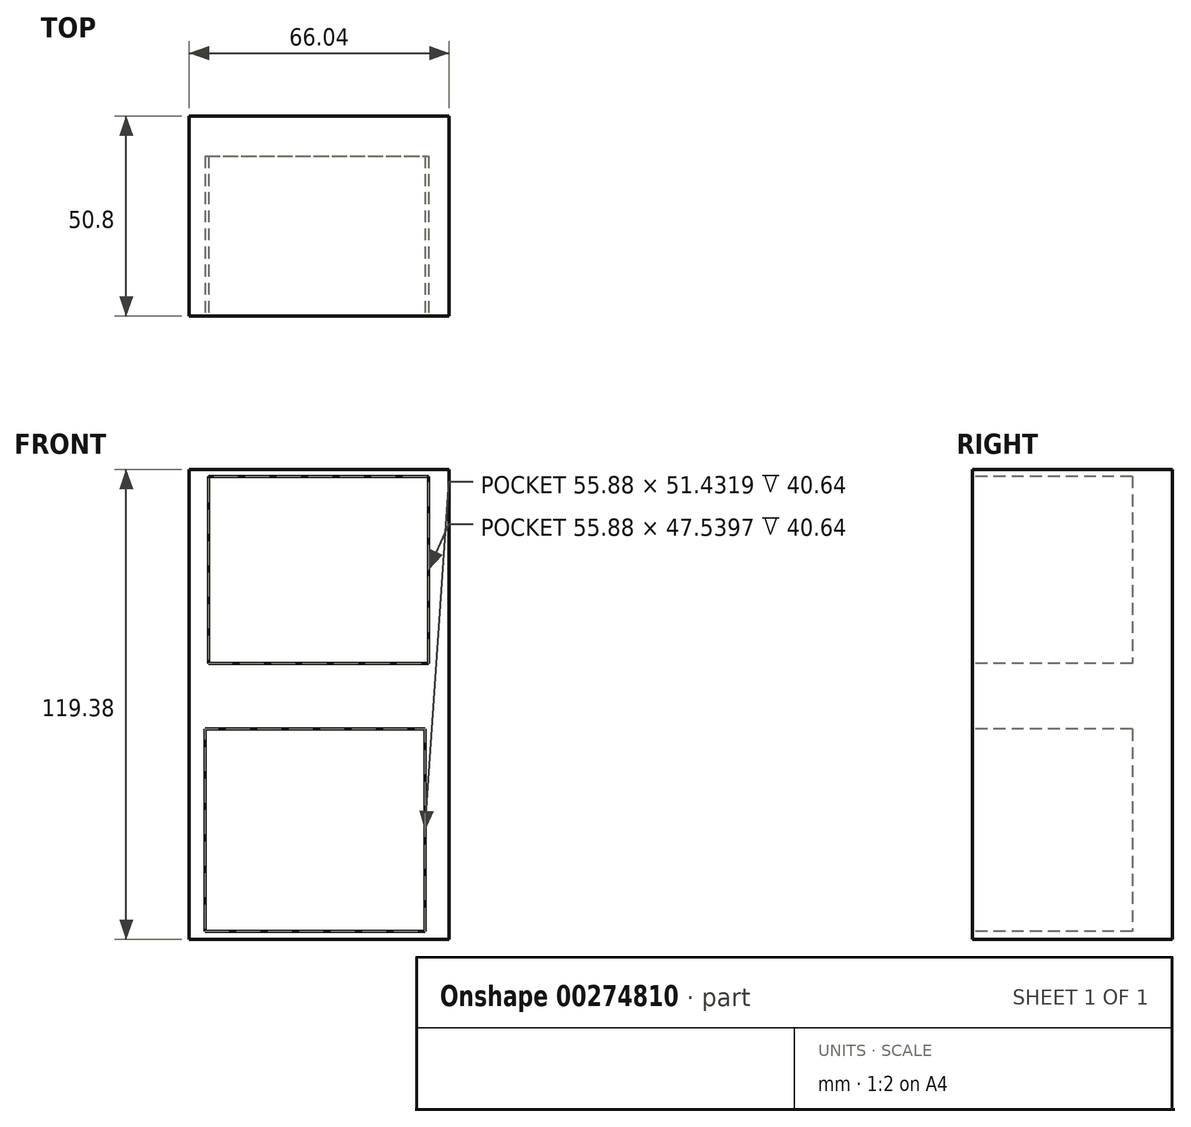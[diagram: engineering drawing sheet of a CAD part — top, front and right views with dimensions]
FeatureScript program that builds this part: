
annotation { "Feature Type Name" : "Feature", "Feature Type Description" : "" }
export const myFeature = defineFeature(function(context is Context, id is Id, definition is map)
    precondition{}
    {
        {
            var Q0;
            Q0=qCreatedBy(makeId("Front.planeOp"),FACE);
            var sketch = newSketch(context, id + "F0", { "sketchPlane" : qUnion([Q0])});
            skLineSegment(sketch, "E0.bottom", {"start": v(33.02, -59.69) * mm, "end": v(-33.02, -59.7) * mm});
            skLineSegment(sketch, "E0.top", {"start": v(33.02, 59.7) * mm, "end": v(-33.02, 59.69) * mm});
            skLineSegment(sketch, "E0.left", {"start": v(33.02, -59.69) * mm, "end": v(33.02, 59.7) * mm});
            skLineSegment(sketch, "E0.right", {"start": v(-33.02, -59.7) * mm, "end": v(-33.02, 59.69) * mm});
            skPoint(sketch, "E0.middle", {"position": v(0, 0) * mm});
            skSolve(sketch);
        }
        {
            var Q0;
            Q0=makeQuery(id+"F0.imprint","IMPRINT",FACE,{"disambiguationData":[TD([[makeQuery(id+"F0.imprint","IMPRINT",EDGE,{"derivedFrom":sQuery(id+"F0.wireOp",EDGE,"E0.bottom")}),-1.0]])]});
            extrude(context, id + "F1", {"entities" : qUnion([Q0]), "depth" : 50.8 * mm});
        }
        {
            var Q0;
            Q0=makeQuery(id+"F1.opExtrude","CAP_FACE",FACE,{"disambiguationData":[OSD([sQuery(id+"F0.wireOp",EDGE,"E0.bottom"),sQuery(id+"F0.wireOp",EDGE,"E0.top"),sQuery(id+"F0.wireOp",EDGE,"E0.left"),sQuery(id+"F0.wireOp",EDGE,"E0.right")])],"isStart":false});
            var sketch = newSketch(context, id + "F2", { "sketchPlane" : qUnion([Q0])});
            skLineSegment(sketch, "E1.bottom", {"start": v(-28.15, 57.96) * mm, "end": v(27.73, 57.96) * mm});
            skLineSegment(sketch, "E1.top", {"start": v(-28.15, 10.42) * mm, "end": v(27.73, 10.42) * mm});
            skLineSegment(sketch, "E1.left", {"start": v(-28.15, 57.96) * mm, "end": v(-28.15, 10.42) * mm});
            skLineSegment(sketch, "E1.right", {"start": v(27.73, 57.96) * mm, "end": v(27.73, 10.42) * mm});
            skLineSegment(sketch, "E2.bottom", {"start": v(-28.98, -6.26) * mm, "end": v(26.9, -6.26) * mm});
            skLineSegment(sketch, "E2.top", {"start": v(-28.98, -57.7) * mm, "end": v(26.9, -57.7) * mm});
            skLineSegment(sketch, "E2.left", {"start": v(-28.98, -6.26) * mm, "end": v(-28.98, -57.7) * mm});
            skLineSegment(sketch, "E2.right", {"start": v(26.9, -6.26) * mm, "end": v(26.9, -57.7) * mm});
            skSolve(sketch);
        }
        {
            var Q0;
            Q0 = qSketchRegion(id + "F2", true);
            extrude(context, id + "F3", {"entities" : qUnion([Q0]), "operationType" : NewBodyOperationType.REMOVE, "oppositeDirection" : true, "depth" : 40.64 * mm});
        }
    });
